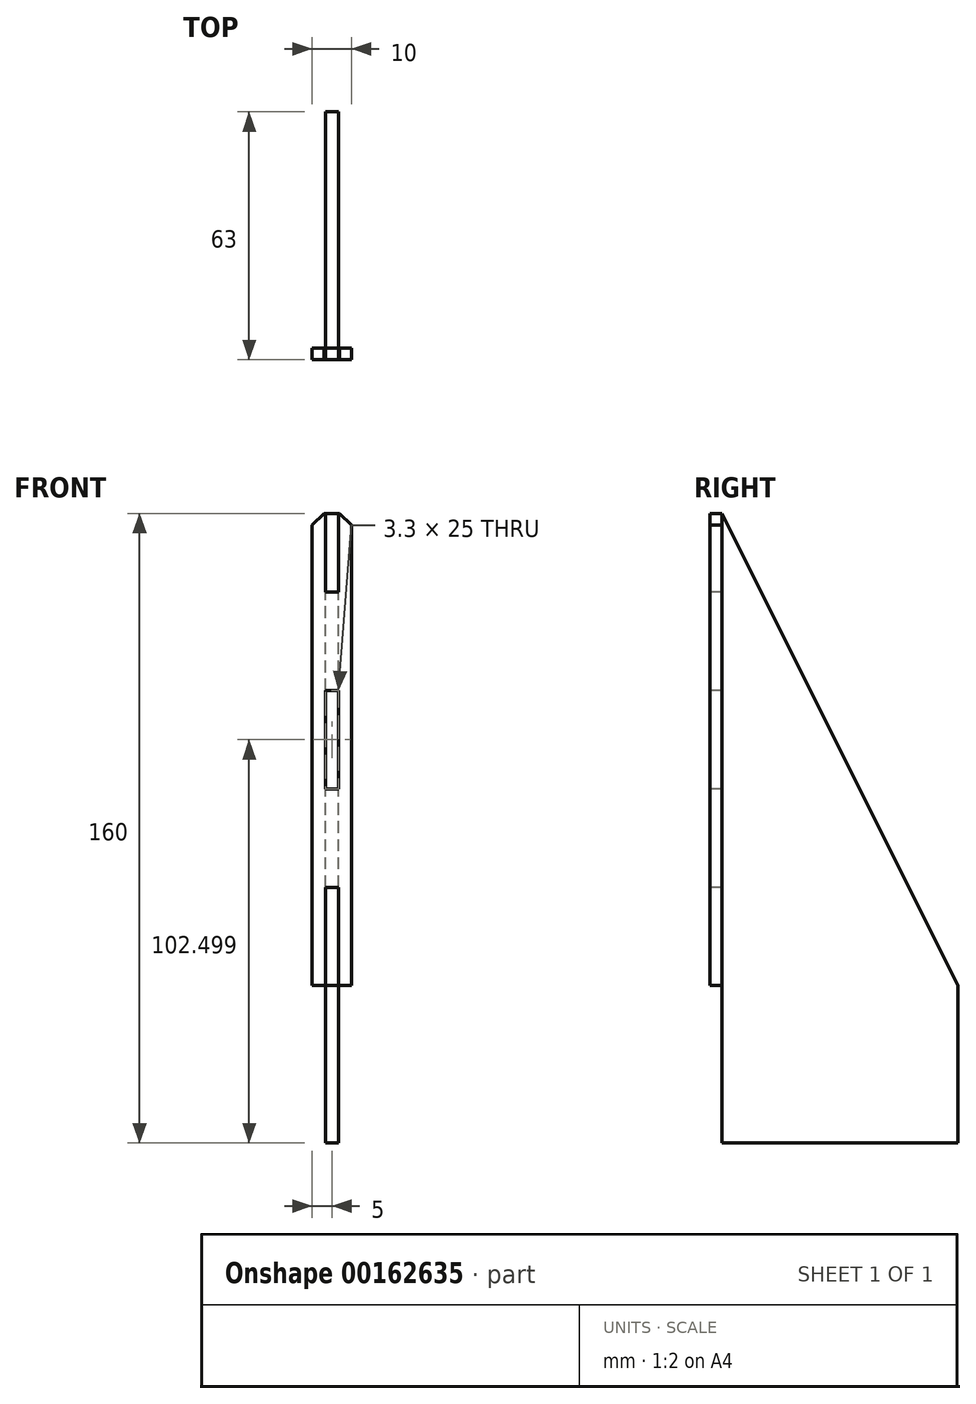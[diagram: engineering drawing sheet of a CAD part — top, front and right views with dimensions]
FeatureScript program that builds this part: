
annotation { "Feature Type Name" : "Feature", "Feature Type Description" : "" }
export const myFeature = defineFeature(function(context is Context, id is Id, definition is map)
    precondition{}
    {
        {
            var Q0;
            Q0=qCreatedBy(makeId("Right.planeOp"),FACE);
            var sketch = newSketch(context, id + "F0", { "sketchPlane" : qUnion([Q0])});
            skLineSegment(sketch, "E0.bottom", {"start": v(0, 0) * mm, "end": v(60, 0) * mm});
            skLineSegment(sketch, "E0.left", {"start": v(0, 0) * mm, "end": v(0, 160) * mm});
            skLineSegment(sketch, "E0.right", {"start": v(60, 0) * mm, "end": v(60, 40) * mm});
            skLineSegment(sketch, "E1", {"start": v(60, 40) * mm, "end": v(0, 40) * mm, "construction": true});
            skLineSegment(sketch, "E2", {"start": v(60, 40) * mm, "end": v(0, 160) * mm});
            skLineSegment(sketch, "E3", {"start": v(0, 40) * mm, "end": v(-3, 40) * mm});
            skLineSegment(sketch, "E4", {"start": v(-3, 40) * mm, "end": v(-3, 160) * mm});
            skLineSegment(sketch, "E5", {"start": v(-3, 160) * mm, "end": v(0, 160) * mm});
            skLineSegment(sketch, "E6.0.1.0", {"start": v(0, 65) * mm, "end": v(-3, 65) * mm});
            skLineSegment(sketch, "E6.0.2.0", {"start": v(0, 90) * mm, "end": v(-3, 90) * mm});
            skLineSegment(sketch, "E6.0.3.0", {"start": v(0, 115) * mm, "end": v(-3, 115) * mm});
            skLineSegment(sketch, "E6.0.4.0", {"start": v(0, 140) * mm, "end": v(-3, 140) * mm});
            skLineSegment(sketch, "E6.direction1", {"start": v(-3, 40) * mm, "end": v(22, 40) * mm, "construction": true});
            skLineSegment(sketch, "E6.direction2", {"start": v(-3, 40) * mm, "end": v(-3, 65) * mm, "construction": true});
            skSolve(sketch);
        }
        {
            var Q0;
            {var subQ3=sQuery(id+"F0.wireOp",EDGE,"E0.bottom");Q0=makeQuery(id+"F0.imprint","IMPRINT",FACE,{"disambiguationData":[TD([[makeQuery(id+"F0.imprint","IMPRINT",EDGE,{"derivedFrom":subQ3}),1.0]])]});}
            var Q1;
            {var subQ0=sQuery(id+"F0.wireOp",EDGE,"E3");Q1=makeQuery(id+"F0.imprint","IMPRINT",FACE,{"disambiguationData":[TD([[makeQuery(id+"F0.imprint","IMPRINT",EDGE,{"derivedFrom":subQ0}),-1.0]])]});}
            var Q2;
            {var subQ0=sQuery(id+"F0.wireOp",EDGE,"E6.0.2.0");Q2=makeQuery(id+"F0.imprint","IMPRINT",FACE,{"disambiguationData":[TD([[makeQuery(id+"F0.imprint","IMPRINT",EDGE,{"derivedFrom":subQ0}),-1.0]])]});}
            var Q3;
            {var subQ0=sQuery(id+"F0.wireOp",EDGE,"E5");Q3=makeQuery(id+"F0.imprint","IMPRINT",FACE,{"disambiguationData":[TD([[makeQuery(id+"F0.imprint","IMPRINT",EDGE,{"derivedFrom":subQ0}),-1.0]])]});}
            extrude(context, id + "F1", {"entities" : qUnion([Q0, Q1, Q2, Q3]), "depth" : 1.65 * mm});
        }
        {
            var Q0;
            Q0=makeQuery(id+"F1.opExtrude","CAP_FACE",FACE,{"disambiguationData":[OSD([sQuery(id+"F0.wireOp",EDGE,"E0.bottom"),sQuery(id+"F0.wireOp",EDGE,"E0.left"),sQuery(id+"F0.wireOp",EDGE,"E0.right"),sQuery(id+"F0.wireOp",EDGE,"E2")])],"isStart":true});
            var Q1;
            Q1=makeQuery(id+"F1.opExtrude","CAP_FACE",FACE,{"disambiguationData":[OSD([sQuery(id+"F0.wireOp",EDGE,"E0.bottom"),sQuery(id+"F0.wireOp",EDGE,"E0.left"),sQuery(id+"F0.wireOp",EDGE,"E0.right"),sQuery(id+"F0.wireOp",EDGE,"E2"),sQuery(id+"F0.wireOp",EDGE,"E3"),sQuery(id+"F0.wireOp",EDGE,"E4"),sQuery(id+"F0.wireOp",EDGE,"E5"),sQuery(id+"F0.wireOp",EDGE,"E6.0.1.0"),sQuery(id+"F0.wireOp",EDGE,"E6.0.2.0"),sQuery(id+"F0.wireOp",EDGE,"E6.0.3.0"),sQuery(id+"F0.wireOp",EDGE,"E6.0.4.0")])],"isStart":false});
            extrude(context, id + "F2", {"entities" : qUnion([Q0, Q1]), "operationType" : NewBodyOperationType.ADD, "depth" : 1.65 * mm});
        }
        {
            var Q0;
            {var subQ0=sQuery(id+"F0.wireOp",EDGE,"E4");var subQ1=makeQuery(id+"F0.imprint","IMPRINT",EDGE,{"disambiguationData":[TD([[makeQuery(id+"F0.imprint","INTERSECT",VERTEX,{"derivedFrom":[sQuery(id+"F0.wireOp",EDGE,"E3"),subQ0]}),-1.0]])],"derivedFrom":subQ0});Q0=makeQuery(id+"F2.boolean.opBoolean","MERGE",FACE,{"derivedFrom":[makeQuery(id+"F1.opExtrude","SWEPT_FACE",FACE,{"disambiguationData":[OSD([subQ0]),TDD([subQ1])]}),makeQuery(id+"F2.opExtrude","SWEPT_FACE",FACE,{"disambiguationData":[OSD([subQ0]),TDD([makeQuery(id+"F1.opExtrude","CAP_EDGE",EDGE,{"disambiguationData":[OSD([subQ0]),TDD([subQ1])],"isStart":true})])]}),makeQuery(id+"F2.opExtrude","SWEPT_FACE",FACE,{"disambiguationData":[OSD([subQ0]),TDD([makeQuery(id+"F1.opExtrude","CAP_EDGE",EDGE,{"disambiguationData":[OSD([subQ0]),TDD([subQ1])],"isStart":false})])]})]});}
            var sketch = newSketch(context, id + "F3", { "sketchPlane" : qUnion([Q0])});
            skLineSegment(sketch, "E7", {"start": v(0, 40) * mm, "end": v(5, 40) * mm});
            skPoint(sketch, "E8.0", {"position": v(0, 160) * mm});
            skLineSegment(sketch, "E9", {"start": v(5, 40) * mm, "end": v(5, 160) * mm});
            skLineSegment(sketch, "E10", {"start": v(5, 160) * mm, "end": v(0, 160) * mm});
            skLineSegment(sketch, "E11.MirrorCS", {"start": v(5, 40) * mm, "end": v(5, -80) * mm});
            skLineSegment(sketch, "E12.MirrorCS", {"start": v(0, 40) * mm, "end": v(-5, 40) * mm});
            skLineSegment(sketch, "E13.MirrorCS", {"start": v(-5, 40) * mm, "end": v(-5, 160) * mm});
            skLineSegment(sketch, "E14.MirrorCS", {"start": v(-5, 160) * mm, "end": v(0, 160) * mm});
            skPoint(sketch, "E15.0", {"position": v(0, 90) * mm});
            skPoint(sketch, "E16.0", {"position": v(0, 140) * mm});
            skLineSegment(sketch, "E17.0", {"start": v(1.65, 40) * mm, "end": v(1.65, 65) * mm});
            skLineSegment(sketch, "E18.0", {"start": v(-1.65, 40) * mm, "end": v(-1.65, 65) * mm});
            skPoint(sketch, "E19.0", {"position": v(0, 65) * mm});
            skLineSegment(sketch, "E20.0", {"start": v(1.65, 90) * mm, "end": v(1.65, 115) * mm});
            skLineSegment(sketch, "E21.0", {"start": v(-1.65, 90) * mm, "end": v(-1.65, 115) * mm});
            skPoint(sketch, "E22.0", {"position": v(0, 115) * mm});
            skLineSegment(sketch, "E23.0", {"start": v(1.65, 115) * mm, "end": v(-1.65, 115) * mm});
            skLineSegment(sketch, "E24.0", {"start": v(1.65, 90) * mm, "end": v(-1.65, 90) * mm});
            skLineSegment(sketch, "E25.0", {"start": v(1.65, 140) * mm, "end": v(1.65, 160) * mm});
            skLineSegment(sketch, "E26.0", {"start": v(1.65, 140) * mm, "end": v(-1.65, 140) * mm});
            skLineSegment(sketch, "E27.0", {"start": v(-1.65, 140) * mm, "end": v(-1.65, 160) * mm});
            skSolve(sketch);
        }
        {
            var Q0;
            {var subQ4=sQuery(id+"F3.wireOp",EDGE,"E9");Q0=makeQuery(id+"F3.imprint","IMPRINT",FACE,{"disambiguationData":[TD([[makeQuery(id+"F3.imprint","IMPRINT",EDGE,{"derivedFrom":subQ4}),1.0]])]});}
            extrude(context, id + "F4", {"entities" : qUnion([Q0]), "oppositeDirection" : true, "depth" : 3 * mm});
        }
        {
            var Q0;
            Q0=makeQuery(id+"F4.opExtrude","SWEPT_EDGE",EDGE,{"disambiguationData":[OSD([sQuery(id+"F3.wireOp",EDGE,"E9"),sQuery(id+"F3.wireOp",EDGE,"E10")])]});
            var Q1;
            Q1=makeQuery(id+"F4.opExtrude","SWEPT_EDGE",EDGE,{"disambiguationData":[OSD([sQuery(id+"F3.wireOp",EDGE,"E13.MirrorCS"),sQuery(id+"F3.wireOp",EDGE,"E14.MirrorCS")])]});
            chamfer(context, id + "F5", {"entities" : qUnion([Q0, Q1]), "width" : 3 * mm, "tangentPropagation" : true});
        }
    });
